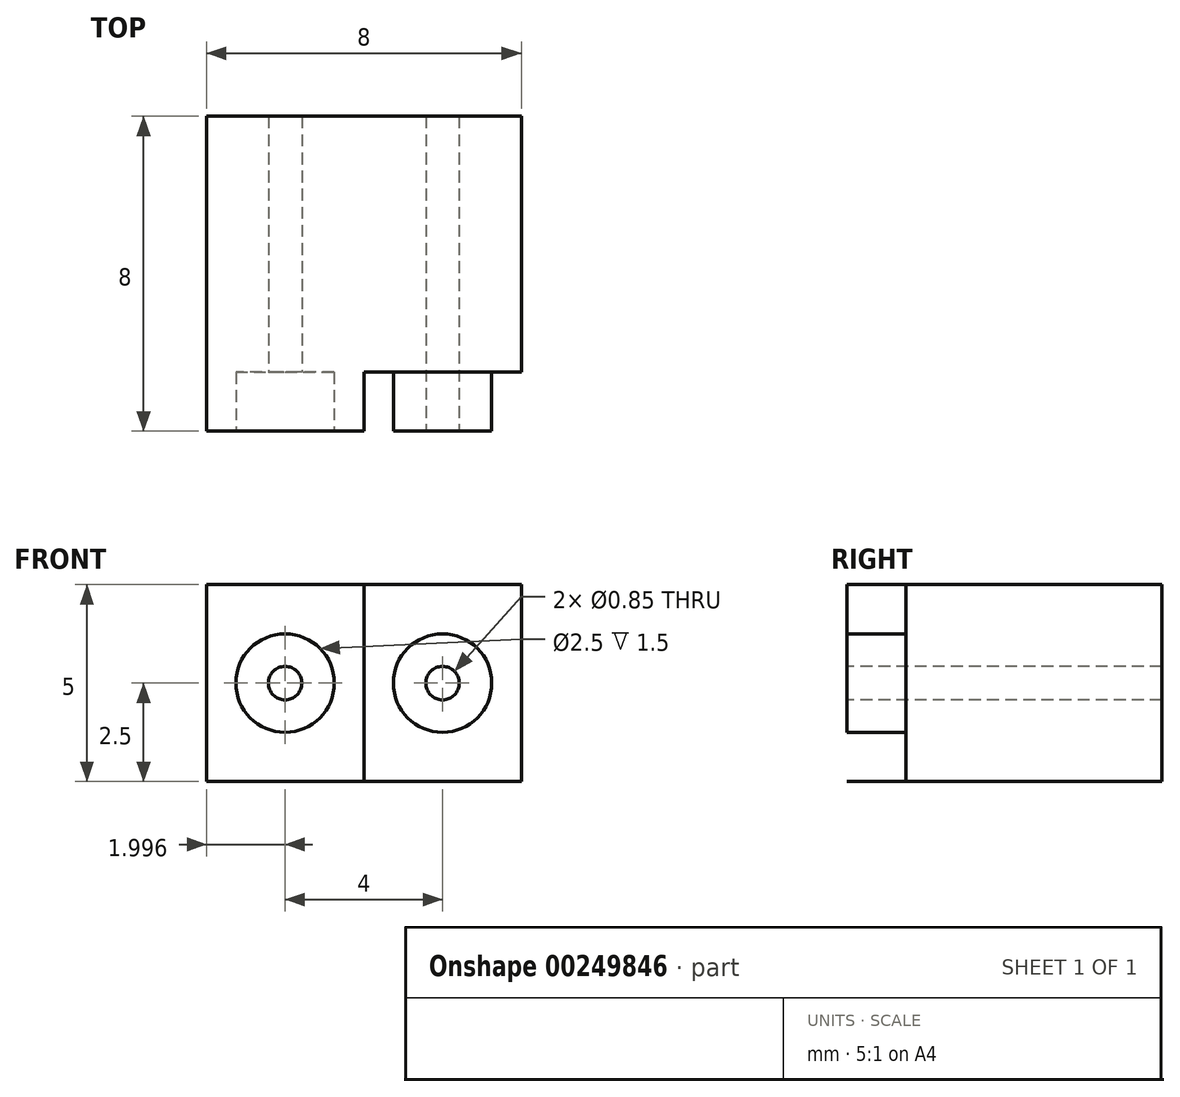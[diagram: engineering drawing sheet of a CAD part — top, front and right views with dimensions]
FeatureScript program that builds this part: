
annotation { "Feature Type Name" : "Feature", "Feature Type Description" : "" }
export const myFeature = defineFeature(function(context is Context, id is Id, definition is map)
    precondition{}
    {
        {
            var Q0;
            Q0=qCreatedBy(makeId("Front.planeOp"),FACE);
            var sketch = newSketch(context, id + "F0", { "sketchPlane" : qUnion([Q0])});
            skLineSegment(sketch, "E0.bottom", {"start": v(-5.86, 0) * mm, "end": v(2.14, 0) * mm});
            skLineSegment(sketch, "E0.top", {"start": v(-5.86, 5) * mm, "end": v(2.14, 5) * mm});
            skLineSegment(sketch, "E0.left", {"start": v(-5.86, 0) * mm, "end": v(-5.86, 5) * mm});
            skLineSegment(sketch, "E0.right", {"start": v(2.14, 0) * mm, "end": v(2.14, 5) * mm});
            skSolve(sketch);
        }
        {
            var Q0;
            Q0=makeQuery(id+"F0.imprint","IMPRINT",FACE,{"disambiguationData":[TD([[makeQuery(id+"F0.imprint","IMPRINT",EDGE,{"derivedFrom":sQuery(id+"F0.wireOp",EDGE,"E0.bottom")}),1.0]])]});
            extrude(context, id + "F1", {"entities" : qUnion([Q0]), "depth" : 8 * mm});
        }
        {
            var Q0;
            Q0=makeQuery(id+"F1.opExtrude","CAP_FACE",FACE,{"disambiguationData":[OSD([sQuery(id+"F0.wireOp",EDGE,"E0.bottom"),sQuery(id+"F0.wireOp",EDGE,"E0.top"),sQuery(id+"F0.wireOp",EDGE,"E0.left"),sQuery(id+"F0.wireOp",EDGE,"E0.right")])],"isStart":false});
            var sketch = newSketch(context, id + "F2", { "sketchPlane" : qUnion([Q0])});
            skLineSegment(sketch, "E1", {"start": v(-1.86, 5) * mm, "end": v(-1.86, 0) * mm});
            skCircle(sketch, "E2", {"center": v(-3.86, 2.5) * mm, "radius": 1.25 * mm});
            skCircle(sketch, "E3.MirrorC", {"center": v(0.14, 2.5) * mm, "radius": 1.25 * mm});
            skSolve(sketch);
        }
        {
            var Q0;
            Q0=makeQuery(id+"F2.imprint","IMPRINT",FACE,{"disambiguationData":[TD([[makeQuery(id+"F2.imprint","IMPRINT",EDGE,{"derivedFrom":sQuery(id+"F2.wireOp",EDGE,"E2")}),1.0]])]});
            extrude(context, id + "F3", {"entities" : qUnion([Q0]), "operationType" : NewBodyOperationType.REMOVE, "oppositeDirection" : true, "depth" : 1.5 * mm});
        }
        {
            var Q0;
            Q0=makeQuery(id+"F2.imprint","IMPRINT",FACE,{"disambiguationData":[TD([[makeQuery(id+"F2.imprint","IMPRINT",EDGE,{"derivedFrom":sQuery(id+"F2.wireOp",EDGE,"E3.MirrorC")}),-1.0]])]});
            extrude(context, id + "F4", {"entities" : qUnion([Q0]), "operationType" : NewBodyOperationType.REMOVE, "oppositeDirection" : true, "depth" : 1.5 * mm});
        }
        {
            var Q0;
            Q0=makeQuery(id+"F1.opExtrude","CAP_FACE",FACE,{"disambiguationData":[OSD([sQuery(id+"F0.wireOp",EDGE,"E0.bottom"),sQuery(id+"F0.wireOp",EDGE,"E0.top"),sQuery(id+"F0.wireOp",EDGE,"E0.left"),sQuery(id+"F0.wireOp",EDGE,"E0.right")])],"isStart":false});
            var sketch = newSketch(context, id + "F5", { "sketchPlane" : qUnion([Q0])});
            skCircle(sketch, "E4", {"center": v(-3.86, 2.5) * mm, "radius": 0.42 * mm});
            skCircle(sketch, "E5", {"center": v(0.14, 2.5) * mm, "radius": 0.42 * mm});
            skSolve(sketch);
        }
        {
            var Q0;
            Q0=makeQuery(id+"F5.imprint","IMPRINT",FACE,{"disambiguationData":[TD([[makeQuery(id+"F5.imprint","IMPRINT",EDGE,{"derivedFrom":sQuery(id+"F5.wireOp",EDGE,"E5")}),1.0]])]});
            extrude(context, id + "F6", {"entities" : qUnion([Q0]), "operationType" : NewBodyOperationType.REMOVE, "oppositeDirection" : true, "depth" : 25 * mm});
        }
        {
            var Q0;
            Q0 = qSketchRegion(id + "F5", true);
            extrude(context, id + "F7", {"entities" : qUnion([Q0]), "operationType" : NewBodyOperationType.REMOVE, "oppositeDirection" : true, "depth" : 25 * mm});
        }
    });
